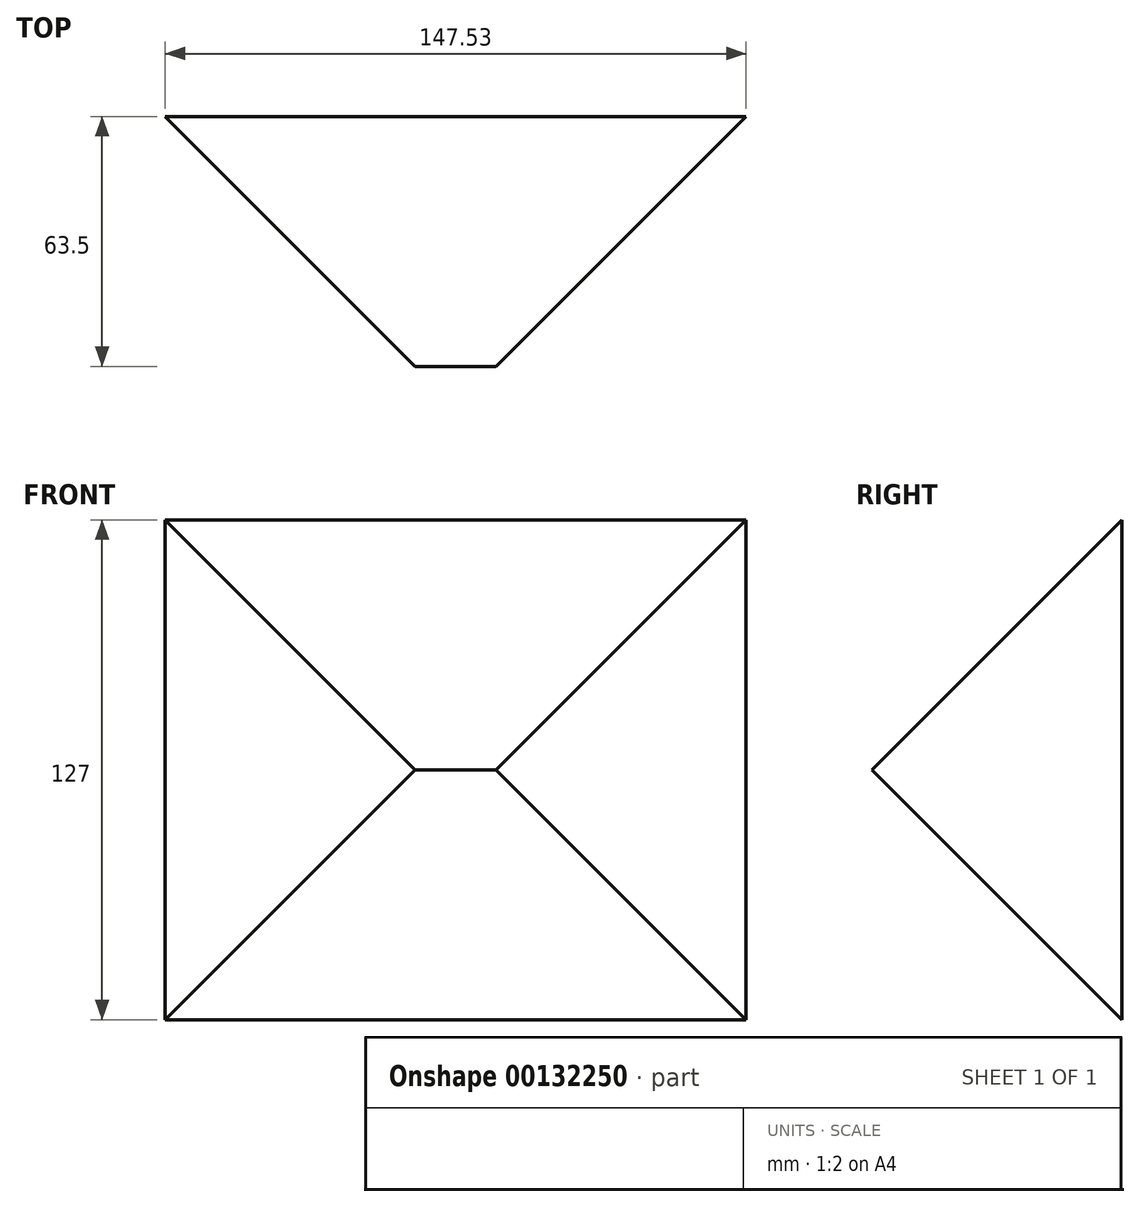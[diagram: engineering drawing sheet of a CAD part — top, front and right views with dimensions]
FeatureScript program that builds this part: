
annotation { "Feature Type Name" : "Feature", "Feature Type Description" : "" }
export const myFeature = defineFeature(function(context is Context, id is Id, definition is map)
    precondition{}
    {
        {
            var Q0;
            Q0=qCreatedBy(makeId("Front.planeOp"),FACE);
            var sketch = newSketch(context, id + "F0", { "sketchPlane" : qUnion([Q0])});
            skLineSegment(sketch, "E0.bottom", {"start": v(75.8, -63.5) * mm, "end": v(-71.73, -63.5) * mm});
            skLineSegment(sketch, "E0.top", {"start": v(75.8, 63.5) * mm, "end": v(-71.73, 63.5) * mm});
            skLineSegment(sketch, "E0.left", {"start": v(75.8, -63.5) * mm, "end": v(75.8, 63.5) * mm});
            skLineSegment(sketch, "E0.right", {"start": v(-71.73, -63.5) * mm, "end": v(-71.73, 63.5) * mm});
            skPoint(sketch, "E0.middle", {"position": v(2.03, 0) * mm});
            skSolve(sketch);
        }
        {
            var Q0;
            Q0 = qSketchRegion(id + "F0", true);
            extrude(context, id + "F1", {"entities" : qUnion([Q0]), "depth" : 254 * mm, "hasDraft" : true, "draftAngle" : 45 * degree, "draftPullDirection" : true});
        }
    });
